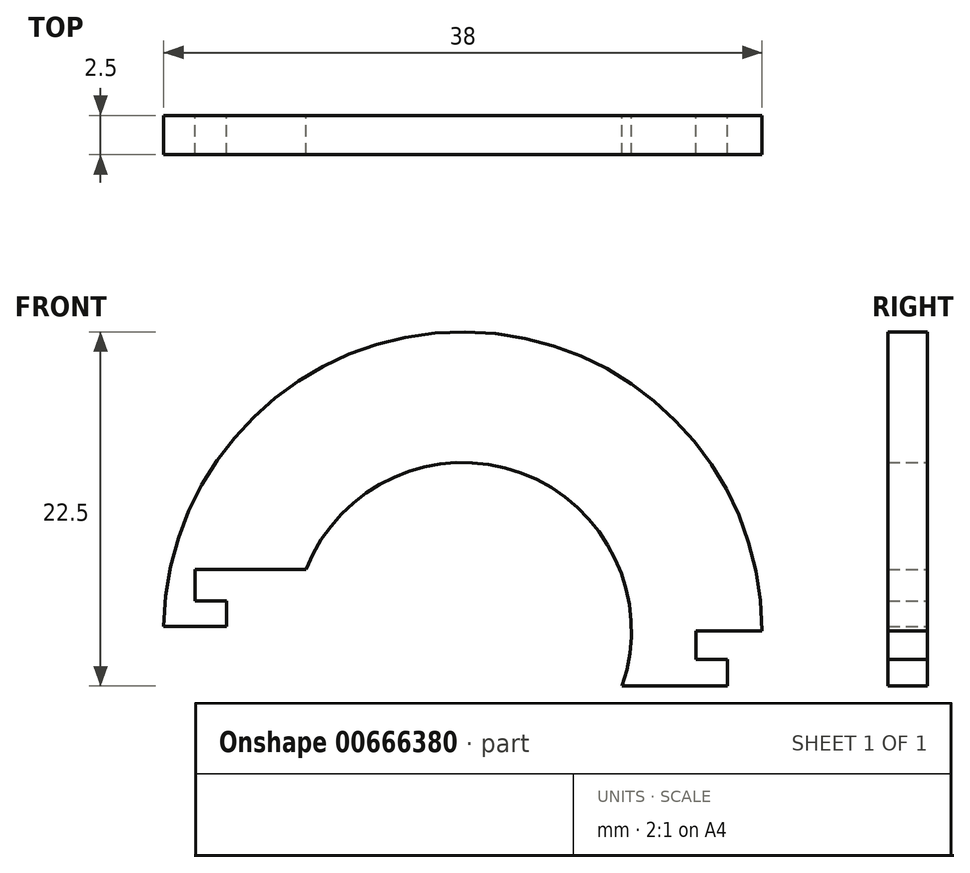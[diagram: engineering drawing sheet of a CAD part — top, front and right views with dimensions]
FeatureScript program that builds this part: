
annotation { "Feature Type Name" : "Feature", "Feature Type Description" : "" }
export const myFeature = defineFeature(function(context is Context, id is Id, definition is map)
    precondition{}
    {
        {
            var Q0;
            Q0=qCreatedBy(makeId("Front.planeOp"),FACE);
            var sketch = newSketch(context, id + "F0", { "sketchPlane" : qUnion([Q0])});
            skLineSegment(sketch, "E0", {"start": v(-19, 0.3) * mm, "end": v(-15, 0.3) * mm});
            skLineSegment(sketch, "E1", {"start": v(-15, 0.3) * mm, "end": v(-15, 1.9) * mm});
            skLineSegment(sketch, "E2", {"start": v(-15, 1.9) * mm, "end": v(-17, 1.9) * mm});
            skLineSegment(sketch, "E3", {"start": v(-17, 1.9) * mm, "end": v(-17, 3.9) * mm});
            skLineSegment(sketch, "E4", {"start": v(-17, 3.9) * mm, "end": v(-9.96, 3.9) * mm});
            skLineSegment(sketch, "E5", {"start": v(19, 0) * mm, "end": v(14.8, 0) * mm});
            skLineSegment(sketch, "E6", {"start": v(14.8, 0) * mm, "end": v(14.8, -1.8) * mm});
            skLineSegment(sketch, "E7", {"start": v(14.8, -1.8) * mm, "end": v(16.8, -1.8) * mm});
            skLineSegment(sketch, "E8", {"start": v(16.8, -1.8) * mm, "end": v(16.8, -3.5) * mm});
            skLineSegment(sketch, "E9", {"start": v(16.8, -3.5) * mm, "end": v(10.11, -3.5) * mm});
            skLineSegment(sketch, "E10", {"start": v(-20.23, 0) * mm, "end": v(29.2, 0) * mm});
            skArc(sketch, "E11", {"start": v(19, 0) * mm, "mid": v(0.15, 19) * mm, "end": v(-19, 0.3) * mm});
            skArc(sketch, "E12", {"start": v(10.11, -3.5) * mm, "mid": v(3.7, 10.04) * mm, "end": v(-9.96, 3.9) * mm});
            skSolve(sketch);
        }
        {
            var Q0;
            Q0 = qSketchRegion(id + "F0", true);
            extrude(context, id + "F1", {"entities" : qUnion([Q0]), "endBound" : BoundingType.SYMMETRIC, "depth" : 2.5 * mm, "offsetDistance" : 25 * mm});
        }
    });
